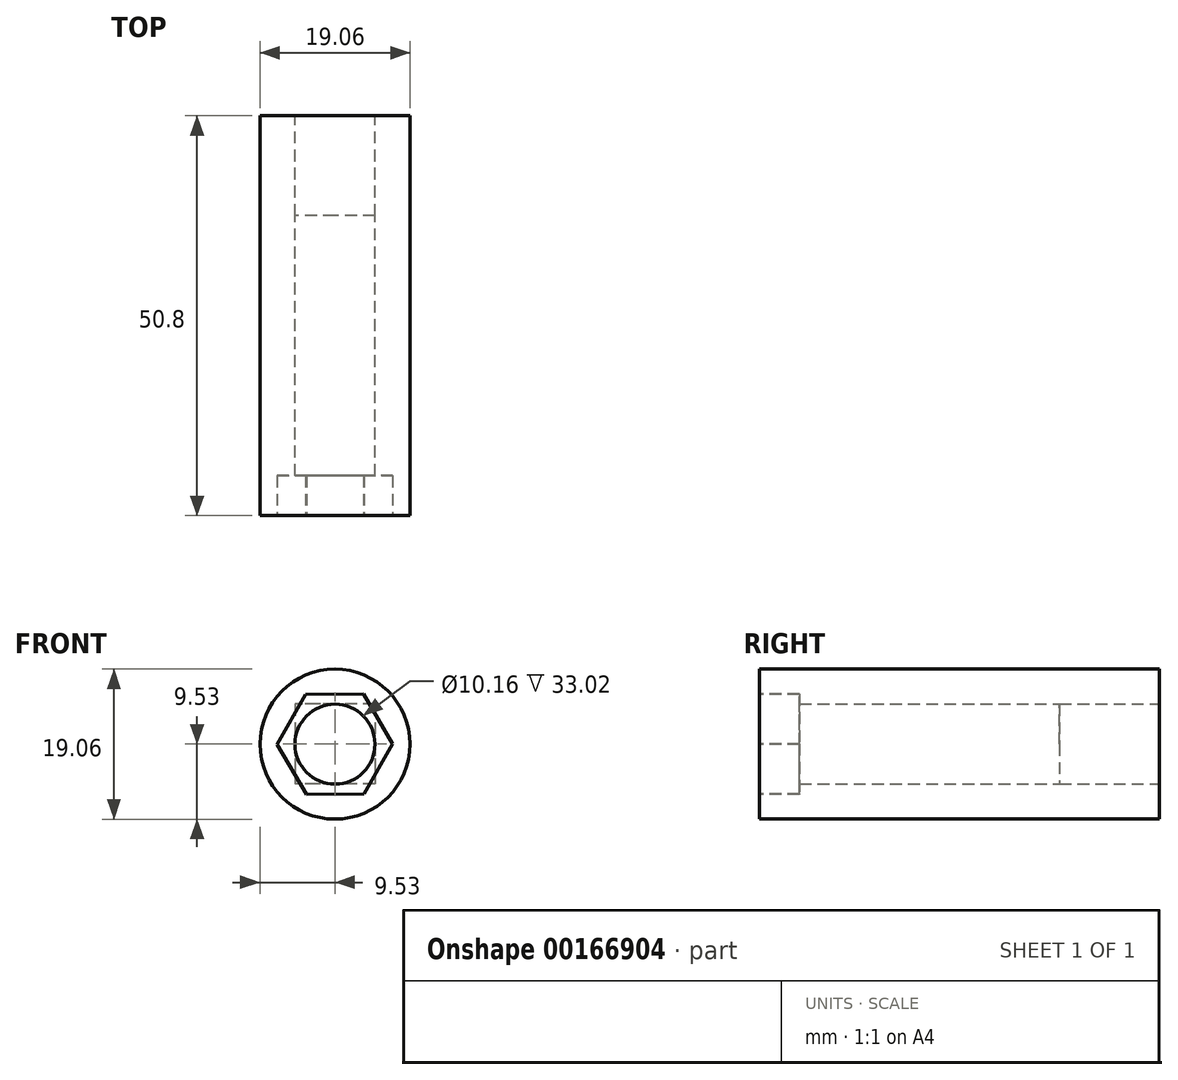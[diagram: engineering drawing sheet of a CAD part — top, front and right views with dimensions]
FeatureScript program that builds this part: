
annotation { "Feature Type Name" : "Feature", "Feature Type Description" : "" }
export const myFeature = defineFeature(function(context is Context, id is Id, definition is map)
    precondition{}
    {
        {
            var Q0;
            Q0=qCreatedBy(makeId("Front.planeOp"),FACE);
            var sketch = newSketch(context, id + "F0", { "sketchPlane" : qUnion([Q0])});
            skCircle(sketch, "E0", {"center": v(0, 0) * mm, "radius": 9.52 * mm});
            skSolve(sketch);
        }
        {
            var Q0;
            Q0=makeQuery(id+"F0.imprint","IMPRINT",FACE,{"disambiguationData":[TD([[makeQuery(id+"F0.imprint","IMPRINT",EDGE,{"derivedFrom":sQuery(id+"F0.wireOp",EDGE,"E0")}),1.0]])]});
            var Q1;
            Q1=sQuery(id+"F0.wireOp",EDGE,"E0");
            extrude(context, id + "F1", {"entities" : qUnion([Q0]), "surfaceEntities" : qUnion([Q1]), "depth" : 50.8 * mm});
        }
        {
            var Q0;
            Q0=qCreatedBy(makeId("Front.planeOp"),FACE);
            var sketch = newSketch(context, id + "F2", { "sketchPlane" : qUnion([Q0])});
            skLineSegment(sketch, "E1.bottom", {"start": v(5.08, 5.08) * mm, "end": v(-5.08, 5.08) * mm});
            skLineSegment(sketch, "E1.top", {"start": v(5.08, -5.08) * mm, "end": v(-5.08, -5.08) * mm});
            skLineSegment(sketch, "E1.left", {"start": v(5.08, 5.08) * mm, "end": v(5.08, -5.08) * mm});
            skLineSegment(sketch, "E1.right", {"start": v(-5.08, 5.08) * mm, "end": v(-5.08, -5.08) * mm});
            skPoint(sketch, "E1.middle", {"position": v(0, 0) * mm});
            skCircle(sketch, "E2", {"center": v(0, 0) * mm, "radius": 5.08 * mm});
            skSolve(sketch);
        }
        {
            var Q0;
            {var subQ0=sQuery(id+"F2.wireOp",EDGE,"E2");var subQ1=makeQuery(id+"F2.imprint","INTERSECT",VERTEX,{"derivedFrom":[sQuery(id+"F2.wireOp",EDGE,"E1.bottom"),subQ0]});Q0=makeQuery(id+"F2.imprint","IMPRINT",FACE,{"disambiguationData":[TD([[makeQuery(id+"F2.imprint","IMPRINT",EDGE,{"disambiguationData":[TD([[subQ1,1.0]])],"derivedFrom":subQ0}),1.0]])]});}
            extrude(context, id + "F3", {"entities" : qUnion([Q0]), "operationType" : NewBodyOperationType.REMOVE, "endBound" : BoundingType.THROUGH_ALL, "depth" : 25.4 * mm});
        }
        {
            var Q0;
            Q0 = qSketchRegion(id + "F2", true);
            extrude(context, id + "F4", {"entities" : qUnion([Q0]), "operationType" : NewBodyOperationType.REMOVE, "depth" : 12.7 * mm});
        }
        {
            var Q0;
            Q0=makeQuery(id+"F1.opExtrude","CAP_FACE",FACE,{"disambiguationData":[OSD([sQuery(id+"F0.wireOp",EDGE,"E0")])],"isStart":false});
            var sketch = newSketch(context, id + "F5", { "sketchPlane" : qUnion([Q0])});
            skCircle(sketch, "E3.cCircle", {"center": v(0, 0) * mm, "radius": 6.35 * mm, "construction": true});
            skLineSegment(sketch, "E3.0", {"start": v(-7.33, -0.05) * mm, "end": v(-3.7, 6.33) * mm});
            skLineSegment(sketch, "E3.1", {"start": v(-3.7, 6.33) * mm, "end": v(3.62, 6.37) * mm});
            skLineSegment(sketch, "E3.2", {"start": v(3.62, 6.37) * mm, "end": v(7.33, 0.05) * mm});
            skLineSegment(sketch, "E3.3", {"start": v(7.33, 0.05) * mm, "end": v(3.7, -6.33) * mm});
            skLineSegment(sketch, "E3.4", {"start": v(3.7, -6.33) * mm, "end": v(-3.62, -6.37) * mm});
            skLineSegment(sketch, "E3.5", {"start": v(-3.62, -6.37) * mm, "end": v(-7.33, -0.05) * mm});
            skPoint(sketch, "E3.0.midPoint", {"position": v(-5.52, 3.14) * mm});
            skSolve(sketch);
        }
        {
            var Q0;
            Q0 = qSketchRegion(id + "F5", true);
            extrude(context, id + "F6", {"entities" : qUnion([Q0]), "operationType" : NewBodyOperationType.REMOVE, "oppositeDirection" : true, "depth" : 5.08 * mm});
        }
    });
